# Revit family: Haws Laboratory Eye-Face Wash 8904
name_source: partatom
category: Plumbing Fixtures
revit_build: Autodesk Revit MEP 2013 (Build: 20130531_2115(x64)
units: mm (PartAtom-declared; Revit-internal decimal feet)

## types (1)
- 8904
    Assembly Code = D2010710
    CW Connection = Yes
    CWFU = 1
    Connection Radius = 1/4"
    Cost Note = For Cost information please visit the Resource tab in the Product Page URL
    Default Elevation = 48"
    Description = 8-foot green hose provides an extended coverage area to further optimize the irrigation process
    Flow = 3.70 GPM
    HW Connection = No
    HWFU = 0
    Hose = Plastic - Haws Corporation - Rubberized Texture
    Hose Length = 96"
    Keynote = 15410
    Manufacturer = Haws Corporation 1455 Kleppe Lane Sparks, NV 89431
    Model = 8904
    Product Documentation Link = http://www.hawsco.com
    Product Page URL = http://www.hawsco.com
    Series = AXION MSR™
    Shower Head = Metal - Haws Corporation - Green Powder Coating
    Shower Head Diam. = 3"
    Tube Height = 9 1/2"
    Tubing = Metal - Haws Corporation - Galvanized Steel
    Type Comments = Unit is activated with simple squeeze lever operation
    URL = http://www.hawsco.com
    Vent Connection = No
    WFU = 1
    Waste Connection = Yes

## geometry (parser evidence)
native form markers: Blend x28, Sweep x2
no freeform markers — native parametric forms only
